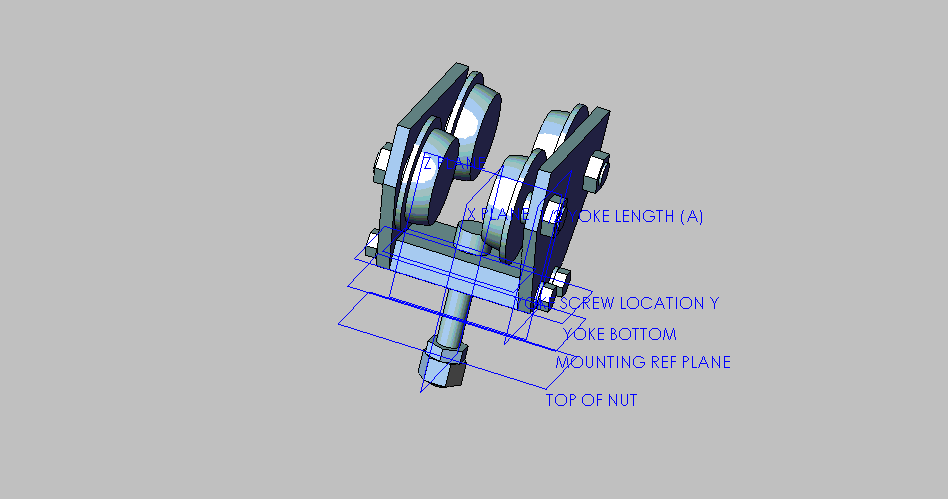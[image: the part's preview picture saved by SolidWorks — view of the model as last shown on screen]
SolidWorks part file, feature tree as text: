
SOLIDWORKS PART (.sldprt)
format: sldprt  version: not decoded by parser v0  size: 1,981,440 bytes
history: native  units: mm
features: sketch x13, extrude x11, plane x10, mirror x5, material x1, chamfer x1, revolve x1, cut_extrude x1 (+10 scaffold rows collapsed)
feature tree (53):
  scaffold x10  (default folders/planes/origin — collapsed)
  material  "Material <not specified>"
  plane  "Z PLANE"  Offset=0mm
  plane  "YOKE BOTTOM"  Offset=0mm
  plane  "X PLANE"  Offset=0mm
  sketch  "YOKE CROSS SECTION"  dims[D1=38.1mm D2=101.6mm]
  plane  "1/2 YOKE LENGTH (A)"  Offset=71.4375mm
  plane  "WHEEL LOCATION"  Offset=95.25mm
  extrude  "YOKE"  [1 undecoded]
  sketch  "SIDEPLATE PROFILE"  dims[c1.D1=~128.517772mm c1.D2=~128.517772mm c1.D3=203.2mm c1.D4=203.2mm c2.D1=50.8mm c2.D2=50.8mm c2.D3=82.55mm c2.D4=82.55mm c2.D5=~128.517772mm c2.D6=~128.517772mm c2.D7=~74.682228mm c2.D8=~74.682228mm c2.D9=266.7mm]
  plane  "WHEEL HEIGHT"  Offset=139.7mm
  plane  "YOKE SCREW LOCATION Z"  Offset=31.75mm
  plane  "YOKE SCREW LOCATION Y"  Offset=19.05mm
  extrude  "SIDEPLATE"  Depth=15.875mm
  sketch  "WHEEL PIN NUT PROFILE"  dims[D1=42.8625mm D2=47.625mm]
  extrude  "WHEEL PIN NUT"  Depth=16.2306mm
  sketch  "WHEEL PIN PROJECTION PROFILE"  dims[D1=28.575mm D2=47.625mm]
  extrude  "WHEEL PIN PROJECTION"  Depth=3.175mm
  sketch  "LOCKNUTS PROFILE"  dims[D1=32.258mm]
  extrude  "LOCKNUTS"  Depth=4.572mm
  sketch  "SCREWS PROFILE"  dims[D1=28.575mm]
  extrude  "SCREWS"  Depth=13.3096mm
  sketch  "PROFILE"  dims[D1=44.45mm]
  extrude  "KING BOLT HEAD"  Depth=25.4mm
  mirror  "Mirror1"
  mirror  "Mirror YOKE SCREWS"
  mirror  "Mirror SIDE 1"
  plane  "TOP OF NUT"  Offset=83.052101mm
  sketch  "DIA."  dims[D1=28.575mm]
  extrude  "KING BOLT"  [1 undecoded]
  sketch  "KING BOLT JAN NUT PROFILE"  dims[D1=42.8752mm]
  extrude  "KING BOLT JAM NUT"  Depth=15.875mm
  sketch  "KING BOLT NUT PROFILE"  dims[c1.D1=46.0375mm c1.D2=44.45mm c2.D1=0.0mm]
  extrude  "KING BOLT NUT"  Depth=28.575mm
  sketch  "Sketch5"
  extrude  "EXTENDED KING BOLT"  Depth=6.35mm
  chamfer  "Chamfer1"  Distance=2.38125mm Angle=45deg
  plane  "MOUNTING REF PLANE"  Offset=34.925mm
  sketch  "Sketch6"  dims[c1.D11=88.9mm c1.D10=88.9mm c1.D1=19.05mm c1.D2=69.85mm c1.D3=~52.954692mm c1.D4=57.15mm c1.D5=69.85mm c1.D6=11.1125mm c1.D7=11.1125mm c1.D8=19.05mm c1.D9=46.0375mm c2.D10=46.0375mm c2.D12=~12.748512mm c2.D1=11.1125mm c2.D2=~17.938894mm c2.D3=19.05mm c2.D4=46.0375mm c2.D5=19.05mm c2.D6=~52.954692mm c2.D7=57.15mm c2.D8=69.85mm c2.D9=69.85mm c2.D11=46.0375mm]
  revolve  "WHEEL"  Angle=360deg
  mirror  "Mirror2"
  mirror  "Mirror3"
  sketch  "Sketch7"  dims[D1=~7.14375mm D2=12.7mm]
  cut_extrude  "COTTER PIN HOLE"  Depth=9.525mm TREADED ROD NUT=9.525mm
decode coverage: 24 of 32 modeling features carry decoded parameters
note: ~ marks probable driven/reference dimensions
note: 2 parameter values undecoded
note: suppression state not decoded; provenance and decode notes live in map.json
